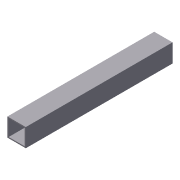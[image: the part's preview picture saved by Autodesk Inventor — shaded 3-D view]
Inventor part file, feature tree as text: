
AUTODESK INVENTOR PART (.ipt)
format: ipt  version: 2012 (Build 160160000, 160)  size: 71,680 bytes
history: native  units: in
note: dims shown in document units (in); Inventor stores cm internally (conversion verified against a paired STEP export)
features: extrude x1, shell x1, sketch x1
ambient origin geometry x8: Origin, YZ Plane, XZ Plane, XY Plane, X Axis, Y Axis, Z Axis, Center Point
bodies: Solid1 (feature_tree)
feature tree (3):
  extrude  "Extrusion1"  Depth=1.0in
  shell  "Shell1"  Thickness=8.0in
  sketch  "Sketch1"  dims[d0=1.0in d1=1.0in d2=8.0in d3=0.0in d4=0.0625in]
